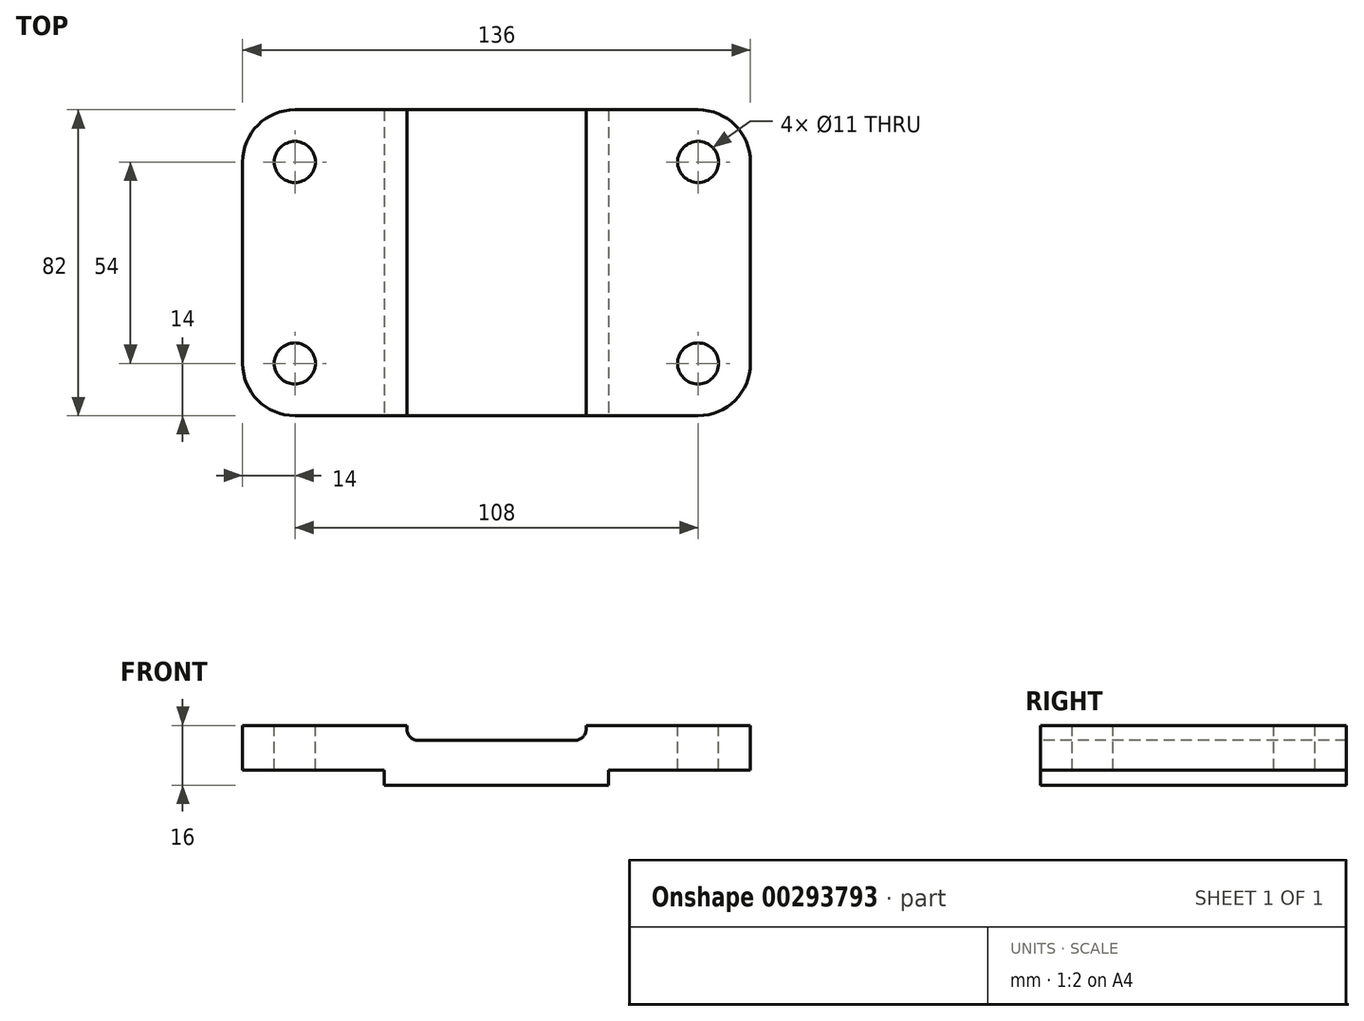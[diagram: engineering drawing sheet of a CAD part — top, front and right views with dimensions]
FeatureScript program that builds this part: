
annotation { "Feature Type Name" : "Feature", "Feature Type Description" : "" }
export const myFeature = defineFeature(function(context is Context, id is Id, definition is map)
    precondition{}
    {
        {
            var Q0;
            Q0=qCreatedBy(makeId("Top.planeOp"),FACE);
            var sketch = newSketch(context, id + "F0", { "sketchPlane" : qUnion([Q0])});
            skLineSegment(sketch, "E0.bottom", {"start": v(14, 0) * mm, "end": v(122, 0) * mm});
            skLineSegment(sketch, "E0.top", {"start": v(14, 82) * mm, "end": v(122, 82) * mm});
            skLineSegment(sketch, "E0.left", {"start": v(0, 14) * mm, "end": v(0, 68) * mm});
            skLineSegment(sketch, "E0.right", {"start": v(136, 14) * mm, "end": v(136, 68) * mm});
            skPoint(sketch, "E1.visualSharp", {"position": v(0, 82) * mm});
            skArc(sketch, "E1.filletArc", {"start": v(14, 82) * mm, "mid": v(4.1, 77.9) * mm, "end": v(0, 68) * mm});
            skPoint(sketch, "E2.visualSharp", {"position": v(136, 82) * mm});
            skArc(sketch, "E2.filletArc", {"start": v(136, 68) * mm, "mid": v(131.9, 77.9) * mm, "end": v(122, 82) * mm});
            skPoint(sketch, "E3.visualSharp", {"position": v(136, 0) * mm});
            skArc(sketch, "E3.filletArc", {"start": v(122, 0) * mm, "mid": v(131.9, 4.1) * mm, "end": v(136, 14) * mm});
            skPoint(sketch, "E4.visualSharp", {"position": v(0, 0) * mm});
            skArc(sketch, "E4.filletArc", {"start": v(0, 14) * mm, "mid": v(4.1, 4.1) * mm, "end": v(14, 0) * mm});
            skLineSegment(sketch, "E5", {"start": v(14, 82) * mm, "end": v(14, 0) * mm, "construction": true});
            skLineSegment(sketch, "E6", {"start": v(0, 14) * mm, "end": v(136, 14) * mm, "construction": true});
            skLineSegment(sketch, "E7", {"start": v(122, 82) * mm, "end": v(122, 0) * mm, "construction": true});
            skLineSegment(sketch, "E8", {"start": v(136, 68) * mm, "end": v(0, 68) * mm, "construction": true});
            skSolve(sketch);
        }
        {
            var Q0;
            Q0=makeQuery(id+"F0.imprint","IMPRINT",FACE,{"disambiguationData":[TD([[makeQuery(id+"F0.imprint","IMPRINT",EDGE,{"derivedFrom":sQuery(id+"F0.wireOp",EDGE,"E0.bottom")}),1.0]])]});
            extrude(context, id + "F1", {"entities" : qUnion([Q0]), "depth" : 16 * mm});
        }
        {
            var Q0;
            Q0=makeQuery(id+"F1.opExtrude","CAP_FACE",FACE,{"disambiguationData":[OSD([sQuery(id+"F0.wireOp",EDGE,"E0.bottom"),sQuery(id+"F0.wireOp",EDGE,"E0.top"),sQuery(id+"F0.wireOp",EDGE,"E0.left"),sQuery(id+"F0.wireOp",EDGE,"E0.right"),sQuery(id+"F0.wireOp",EDGE,"E1.filletArc"),sQuery(id+"F0.wireOp",EDGE,"E2.filletArc"),sQuery(id+"F0.wireOp",EDGE,"E3.filletArc"),sQuery(id+"F0.wireOp",EDGE,"E4.filletArc")])],"isStart":false});
            var sketch = newSketch(context, id + "F2", { "sketchPlane" : qUnion([Q0])});
            skLineSegment(sketch, "E9", {"start": v(0, 68) * mm, "end": v(136, 68) * mm, "construction": true});
            skLineSegment(sketch, "E10", {"start": v(122, 82) * mm, "end": v(122, 0) * mm, "construction": true});
            skLineSegment(sketch, "E11", {"start": v(136, 14) * mm, "end": v(0, 14) * mm, "construction": true});
            skLineSegment(sketch, "E12", {"start": v(14, 82) * mm, "end": v(14, 0) * mm, "construction": true});
            skCircle(sketch, "E13", {"center": v(14, 68) * mm, "radius": 5.5 * mm});
            skCircle(sketch, "E14", {"center": v(14, 14) * mm, "radius": 5.5 * mm});
            skCircle(sketch, "E15.1.0.0", {"center": v(122, 68) * mm, "radius": 5.5 * mm});
            skCircle(sketch, "E15.1.0.1", {"center": v(122, 14) * mm, "radius": 5.5 * mm});
            skLineSegment(sketch, "E15.direction1", {"start": v(14, 68) * mm, "end": v(122, 68) * mm, "construction": true});
            skSolve(sketch);
        }
        {
            var Q0;
            Q0 = qSketchRegion(id + "F2", true);
            extrude(context, id + "F3", {"entities" : qUnion([Q0]), "operationType" : NewBodyOperationType.REMOVE, "endBound" : BoundingType.THROUGH_ALL, "oppositeDirection" : true, "depth" : 25 * mm});
        }
        {
            var Q0;
            Q0=makeQuery(id+"F1.opExtrude","SWEPT_FACE",FACE,{"disambiguationData":[OSD([sQuery(id+"F0.wireOp",EDGE,"E0.bottom")])]});
            var sketch = newSketch(context, id + "F4", { "sketchPlane" : qUnion([Q0])});
            skLineSegment(sketch, "E16.bottom", {"start": v(0, 0) * mm, "end": v(38, 0) * mm});
            skLineSegment(sketch, "E16.top", {"start": v(0, 4) * mm, "end": v(38, 4) * mm});
            skLineSegment(sketch, "E16.left", {"start": v(0, 0) * mm, "end": v(0, 4) * mm});
            skLineSegment(sketch, "E16.right", {"start": v(38, 0) * mm, "end": v(38, 4) * mm});
            skLineSegment(sketch, "E17.bottom", {"start": v(136, 0) * mm, "end": v(98, 0) * mm});
            skLineSegment(sketch, "E17.top", {"start": v(136, 4) * mm, "end": v(98, 4) * mm});
            skLineSegment(sketch, "E17.left", {"start": v(136, 0) * mm, "end": v(136, 4) * mm});
            skLineSegment(sketch, "E17.right", {"start": v(98, 0) * mm, "end": v(98, 4) * mm});
            skSolve(sketch);
        }
        {
            var Q0;
            Q0 = qSketchRegion(id + "F4", true);
            extrude(context, id + "F5", {"entities" : qUnion([Q0]), "operationType" : NewBodyOperationType.REMOVE, "endBound" : BoundingType.THROUGH_ALL, "oppositeDirection" : true, "depth" : 25 * mm});
        }
        {
            var Q0;
            Q0=makeQuery(id+"F1.opExtrude","SWEPT_FACE",FACE,{"disambiguationData":[OSD([sQuery(id+"F0.wireOp",EDGE,"E0.bottom")])]});
            var sketch = newSketch(context, id + "F6", { "sketchPlane" : qUnion([Q0])});
            skLineSegment(sketch, "E18.bottom", {"start": v(44, 16) * mm, "end": v(92, 16) * mm});
            skLineSegment(sketch, "E18.top", {"start": v(44, 12) * mm, "end": v(92, 12) * mm});
            skLineSegment(sketch, "E18.left", {"start": v(44, 16) * mm, "end": v(44, 12) * mm});
            skLineSegment(sketch, "E18.right", {"start": v(92, 16) * mm, "end": v(92, 12) * mm});
            skSolve(sketch);
        }
        {
            var Q0;
            Q0 = qSketchRegion(id + "F6", true);
            extrude(context, id + "F7", {"entities" : qUnion([Q0]), "operationType" : NewBodyOperationType.REMOVE, "endBound" : BoundingType.THROUGH_ALL, "oppositeDirection" : true, "depth" : 25 * mm});
        }
        {
            var Q0;
            Q0=makeQuery(id+"F7.boolean.opBoolean","COPY",EDGE,{"derivedFrom":makeQuery(id+"F7.opExtrude","SWEPT_EDGE",EDGE,{"disambiguationData":[OSD([sQuery(id+"F6.wireOp",EDGE,"E18.top"),sQuery(id+"F6.wireOp",EDGE,"E18.left")])]})});
            fillet(context, id + "F8", {"entities" : qUnion([Q0]), "radius" : 3 * mm, "tangentPropagation" : true, "allowEdgeOverflow" : false});
        }
        {
            var Q0;
            Q0=makeQuery(id+"F7.boolean.opBoolean","COPY",EDGE,{"derivedFrom":makeQuery(id+"F7.opExtrude","SWEPT_EDGE",EDGE,{"disambiguationData":[OSD([sQuery(id+"F6.wireOp",EDGE,"E18.top"),sQuery(id+"F6.wireOp",EDGE,"E18.right")])]})});
            fillet(context, id + "F9", {"entities" : qUnion([Q0]), "radius" : 3 * mm, "tangentPropagation" : true, "allowEdgeOverflow" : false});
        }
    });
